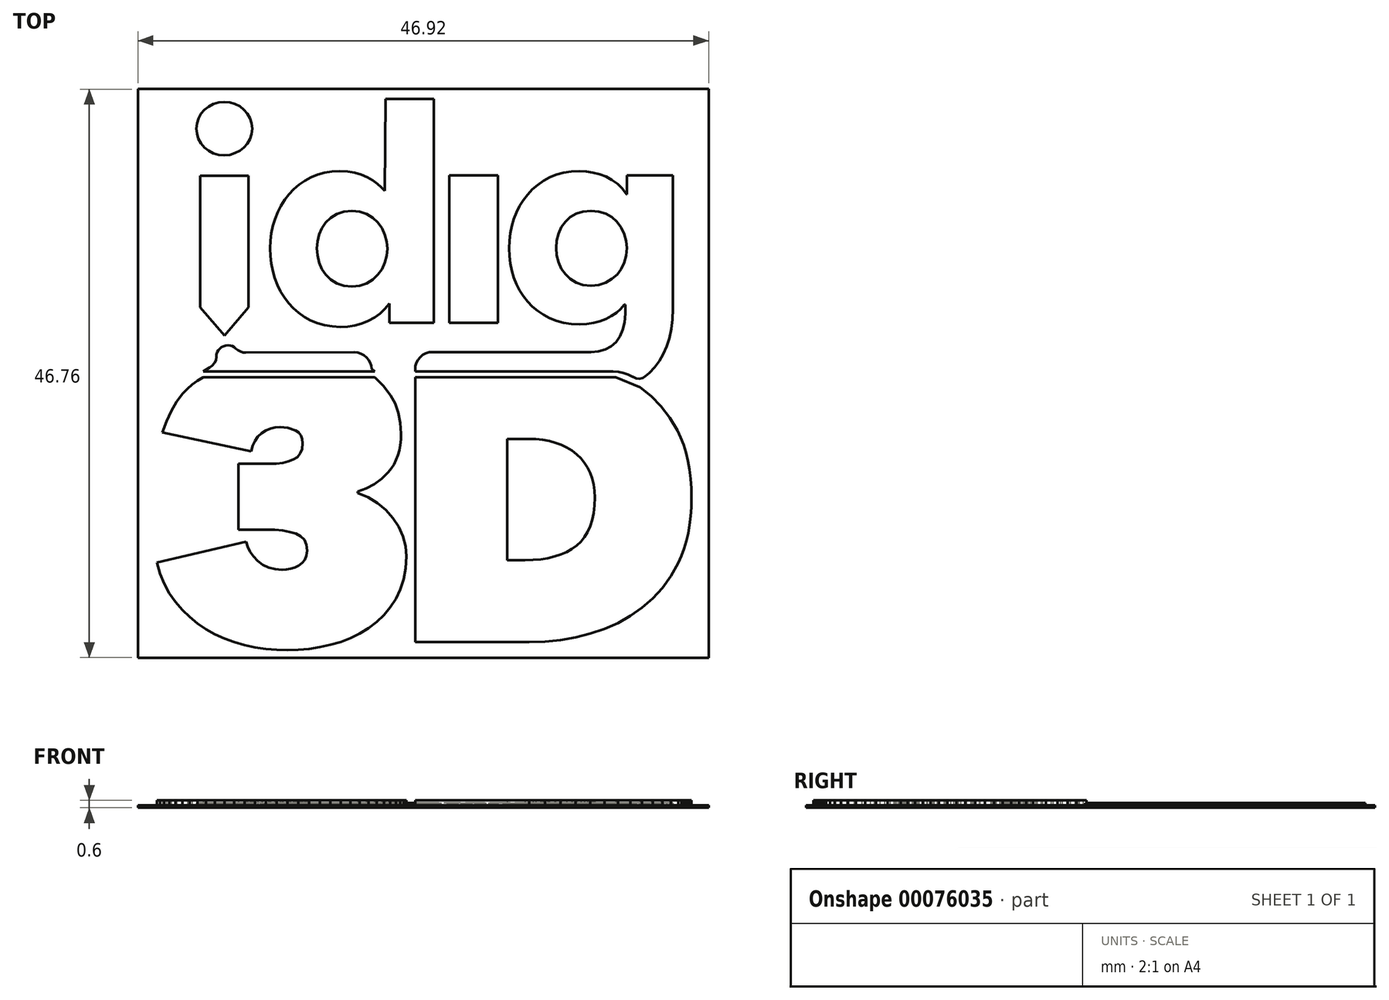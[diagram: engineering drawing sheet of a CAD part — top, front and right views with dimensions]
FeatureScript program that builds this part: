
annotation { "Feature Type Name" : "Feature", "Feature Type Description" : "" }
export const myFeature = defineFeature(function(context is Context, id is Id, definition is map)
    precondition{}
    {
        {
            var Q0;
            Q0=qCreatedBy(makeId("Top.planeOp"),FACE);
            var sketch = newSketch(context, id + "F0", { "sketchPlane" : qUnion([Q0])});
            skLineSegment(sketch, "E0", {"start": v(-3.12, 22.59) * mm, "end": v(0.88, 22.59) * mm});
            skLineSegment(sketch, "E1", {"start": v(0.88, 22.59) * mm, "end": v(0.88, 4.17) * mm});
            skLineSegment(sketch, "E2", {"start": v(17.03, -19.95) * mm, "end": v(16, -20.53) * mm});
            skLineSegment(sketch, "E3", {"start": v(12.5, -21.71) * mm, "end": v(11.27, -21.93) * mm});
            skLineSegment(sketch, "E4", {"start": v(14.9, -21.01) * mm, "end": v(13.73, -21.4) * mm});
            skLineSegment(sketch, "E5", {"start": v(-0.67, -22.1) * mm, "end": v(8.7, -22.1) * mm});
            skLineSegment(sketch, "E6", {"start": v(-3.17, 15) * mm, "end": v(-3.12, 22.59) * mm});
            skLineSegment(sketch, "E7", {"start": v(10, -22.06) * mm, "end": v(8.7, -22.1) * mm});
            skLineSegment(sketch, "E8", {"start": v(17.99, -19.28) * mm, "end": v(17.03, -19.95) * mm});
            skLineSegment(sketch, "E9", {"start": v(-21.3, -17.31) * mm, "end": v(-21.64, -16.47) * mm});
            skLineSegment(sketch, "E10", {"start": v(16, -20.53) * mm, "end": v(14.9, -21.01) * mm});
            skLineSegment(sketch, "E11", {"start": v(13.73, -21.4) * mm, "end": v(12.5, -21.71) * mm});
            skLineSegment(sketch, "E12", {"start": v(11.27, -21.93) * mm, "end": v(10, -22.06) * mm});
            skLineSegment(sketch, "E13", {"start": v(19.65, -17.64) * mm, "end": v(18.86, -18.5) * mm});
            skLineSegment(sketch, "E14", {"start": v(-18.56, -20.57) * mm, "end": v(-19.21, -20.04) * mm});
            skLineSegment(sketch, "E15", {"start": v(-16.35, -21.82) * mm, "end": v(-17.13, -21.46) * mm});
            skLineSegment(sketch, "E16", {"start": v(-11.18, -22.76) * mm, "end": v(-12.07, -22.74) * mm});
            skLineSegment(sketch, "E17", {"start": v(-9.4, -22.65) * mm, "end": v(-10.29, -22.73) * mm});
            skLineSegment(sketch, "E18", {"start": v(-7.64, -22.33) * mm, "end": v(-8.52, -22.52) * mm});
            skLineSegment(sketch, "E19", {"start": v(-15.54, -22.11) * mm, "end": v(-16.35, -21.82) * mm});
            skLineSegment(sketch, "E20", {"start": v(-0.67, -22.1) * mm, "end": v(-0.67, -0.31) * mm});
            skLineSegment(sketch, "E21", {"start": v(-10.29, -22.73) * mm, "end": v(-11.18, -22.76) * mm});
            skLineSegment(sketch, "E22", {"start": v(-5.98, -21.78) * mm, "end": v(-6.8, -22.09) * mm});
            skLineSegment(sketch, "E23", {"start": v(21.43, -14.42) * mm, "end": v(21.2, -15.02) * mm});
            skLineSegment(sketch, "E24", {"start": v(20.94, -15.6) * mm, "end": v(20.34, -16.67) * mm});
            skLineSegment(sketch, "E25", {"start": v(-14.7, -22.35) * mm, "end": v(-15.54, -22.11) * mm});
            skLineSegment(sketch, "E26", {"start": v(21.9, -12.46) * mm, "end": v(21.77, -13.14) * mm});
            skLineSegment(sketch, "E27", {"start": v(-20.38, -18.8) * mm, "end": v(-20.87, -18.09) * mm});
            skLineSegment(sketch, "E28", {"start": v(21.4, -5.87) * mm, "end": v(21.6, -6.52) * mm});
            skLineSegment(sketch, "E29", {"start": v(21.89, -7.91) * mm, "end": v(21.98, -8.66) * mm});
            skLineSegment(sketch, "E30", {"start": v(22.03, -9.45) * mm, "end": v(22.05, -10.28) * mm});
            skLineSegment(sketch, "E31", {"start": v(-21.64, -16.47) * mm, "end": v(-21.91, -15.56) * mm});
            skLineSegment(sketch, "E32", {"start": v(-21.91, -15.56) * mm, "end": v(-14.58, -13.84) * mm});
            skLineSegment(sketch, "E33", {"start": v(21.2, -15.02) * mm, "end": v(20.94, -15.6) * mm});
            skLineSegment(sketch, "E34", {"start": v(-6.8, -22.09) * mm, "end": v(-7.64, -22.33) * mm});
            skLineSegment(sketch, "E35", {"start": v(-13.82, -22.53) * mm, "end": v(-14.7, -22.35) * mm});
            skLineSegment(sketch, "E36", {"start": v(20.34, -16.67) * mm, "end": v(19.65, -17.64) * mm});
            skLineSegment(sketch, "E37", {"start": v(-8.52, -22.52) * mm, "end": v(-9.4, -22.65) * mm});
            skLineSegment(sketch, "E38", {"start": v(-19.21, -20.04) * mm, "end": v(-19.82, -19.45) * mm});
            skLineSegment(sketch, "E39", {"start": v(22.03, -11.03) * mm, "end": v(21.98, -11.76) * mm});
            skLineSegment(sketch, "E40", {"start": v(21.6, -6.52) * mm, "end": v(21.76, -7.2) * mm});
            skLineSegment(sketch, "E41", {"start": v(21.77, -13.14) * mm, "end": v(21.62, -13.8) * mm});
            skLineSegment(sketch, "E42", {"start": v(21.76, -7.2) * mm, "end": v(21.89, -7.91) * mm});
            skLineSegment(sketch, "E43", {"start": v(21.98, -8.66) * mm, "end": v(22.03, -9.45) * mm});
            skLineSegment(sketch, "E44", {"start": v(-20.87, -18.09) * mm, "end": v(-21.3, -17.31) * mm});
            skLineSegment(sketch, "E45", {"start": v(-12.95, -22.66) * mm, "end": v(-13.82, -22.53) * mm});
            skLineSegment(sketch, "E46", {"start": v(-17.87, -21.04) * mm, "end": v(-18.56, -20.57) * mm});
            skLineSegment(sketch, "E47", {"start": v(-3.84, -20.46) * mm, "end": v(-4.5, -20.96) * mm});
            skLineSegment(sketch, "E48", {"start": v(21.62, -13.8) * mm, "end": v(21.43, -14.42) * mm});
            skLineSegment(sketch, "E49", {"start": v(-5.22, -21.4) * mm, "end": v(-5.98, -21.78) * mm});
            skLineSegment(sketch, "E50", {"start": v(21.16, -5.27) * mm, "end": v(21.4, -5.87) * mm});
            skLineSegment(sketch, "E51", {"start": v(-19.82, -19.45) * mm, "end": v(-20.38, -18.8) * mm});
            skLineSegment(sketch, "E52", {"start": v(22.05, -10.28) * mm, "end": v(22.03, -11.03) * mm});
            skLineSegment(sketch, "E53", {"start": v(-12.07, -22.74) * mm, "end": v(-12.95, -22.66) * mm});
            skLineSegment(sketch, "E54", {"start": v(-1.68, -13.4) * mm, "end": v(-1.47, -14.21) * mm});
            skLineSegment(sketch, "E55", {"start": v(13.5, -13.04) * mm, "end": v(13.72, -12.57) * mm});
            skLineSegment(sketch, "E56", {"start": v(-1.4, -15.03) * mm, "end": v(-1.45, -16.02) * mm});
            skLineSegment(sketch, "E57", {"start": v(9.02, -15.34) * mm, "end": v(9.65, -15.29) * mm});
            skLineSegment(sketch, "E58", {"start": v(-1.62, -16.94) * mm, "end": v(-1.88, -17.78) * mm});
            skLineSegment(sketch, "E59", {"start": v(-17.13, -21.46) * mm, "end": v(-17.87, -21.04) * mm});
            skLineSegment(sketch, "E60", {"start": v(13.25, -13.46) * mm, "end": v(13.5, -13.04) * mm});
            skLineSegment(sketch, "E61", {"start": v(6.89, -15.36) * mm, "end": v(8.34, -15.36) * mm});
            skLineSegment(sketch, "E62", {"start": v(10.8, -15.06) * mm, "end": v(11.3, -14.9) * mm});
            skLineSegment(sketch, "E63", {"start": v(-2.26, -18.55) * mm, "end": v(-2.72, -19.25) * mm});
            skLineSegment(sketch, "E64", {"start": v(6.89, -5.39) * mm, "end": v(6.89, -15.36) * mm});
            skLineSegment(sketch, "E65", {"start": v(-3.25, -19.89) * mm, "end": v(-3.84, -20.46) * mm});
            skLineSegment(sketch, "E66", {"start": v(18.86, -18.5) * mm, "end": v(17.99, -19.28) * mm});
            skLineSegment(sketch, "E67", {"start": v(21.98, -11.76) * mm, "end": v(21.9, -12.46) * mm});
            skLineSegment(sketch, "E68", {"start": v(-4.5, -20.96) * mm, "end": v(-5.22, -21.4) * mm});
            skLineSegment(sketch, "E69", {"start": v(-1.98, -6.33) * mm, "end": v(-2.1, -6.74) * mm});
            skLineSegment(sketch, "E70", {"start": v(-14.75, 21.7) * mm, "end": v(-14.47, 21.38) * mm});
            skLineSegment(sketch, "E71", {"start": v(13.88, -12.05) * mm, "end": v(14, -11.49) * mm});
            skLineSegment(sketch, "E72", {"start": v(-18, 21.67) * mm, "end": v(-17.66, 21.94) * mm});
            skLineSegment(sketch, "E73", {"start": v(-17.27, 22.15) * mm, "end": v(-16.84, 22.28) * mm});
            skLineSegment(sketch, "E74", {"start": v(-2.72, -19.25) * mm, "end": v(-3.25, -19.89) * mm});
            skLineSegment(sketch, "E75", {"start": v(12.21, -14.44) * mm, "end": v(12.6, -14.16) * mm});
            skLineSegment(sketch, "E76", {"start": v(9.65, -15.29) * mm, "end": v(10.24, -15.2) * mm});
            skLineSegment(sketch, "E77", {"start": v(10.24, -15.2) * mm, "end": v(10.8, -15.06) * mm});
            skLineSegment(sketch, "E78", {"start": v(11.3, -14.9) * mm, "end": v(11.78, -14.69) * mm});
            skLineSegment(sketch, "E79", {"start": v(11.78, -14.69) * mm, "end": v(12.21, -14.44) * mm});
            skLineSegment(sketch, "E80", {"start": v(12.22, -6.36) * mm, "end": v(11.8, -6.1) * mm});
            skLineSegment(sketch, "E81", {"start": v(13.25, -7.36) * mm, "end": v(12.95, -7) * mm});
            skLineSegment(sketch, "E82", {"start": v(-18.66, 20.14) * mm, "end": v(-18.61, 20.57) * mm});
            skLineSegment(sketch, "E83", {"start": v(13.72, -12.57) * mm, "end": v(13.88, -12.05) * mm});
            skLineSegment(sketch, "E84", {"start": v(10.36, -5.57) * mm, "end": v(9.82, -5.47) * mm});
            skLineSegment(sketch, "E85", {"start": v(14.07, -10.87) * mm, "end": v(14.09, -10.21) * mm});
            skLineSegment(sketch, "E86", {"start": v(-15.91, 22.29) * mm, "end": v(-15.48, 22.16) * mm});
            skLineSegment(sketch, "E87", {"start": v(-1.88, -17.78) * mm, "end": v(-2.26, -18.55) * mm});
            skLineSegment(sketch, "E88", {"start": v(-17.26, 18.1) * mm, "end": v(-17.65, 18.3) * mm});
            skLineSegment(sketch, "E89", {"start": v(-16.84, 17.98) * mm, "end": v(-17.26, 18.1) * mm});
            skLineSegment(sketch, "E90", {"start": v(14.09, -10.21) * mm, "end": v(14.07, -9.66) * mm});
            skLineSegment(sketch, "E91", {"start": v(-14.26, 21) * mm, "end": v(-14.12, 20.58) * mm});
            skLineSegment(sketch, "E92", {"start": v(-18.28, 21.35) * mm, "end": v(-18, 21.67) * mm});
            skLineSegment(sketch, "E93", {"start": v(12.6, -14.16) * mm, "end": v(12.95, -13.83) * mm});
            skLineSegment(sketch, "E94", {"start": v(8.64, -5.39) * mm, "end": v(6.89, -5.39) * mm});
            skLineSegment(sketch, "E95", {"start": v(-14.37, 16.26) * mm, "end": v(-14.37, 5.44) * mm});
            skLineSegment(sketch, "E96", {"start": v(-18.36, 16.26) * mm, "end": v(-14.37, 16.26) * mm});
            skLineSegment(sketch, "E97", {"start": v(-18.36, 5.44) * mm, "end": v(-18.36, 16.26) * mm});
            skLineSegment(sketch, "E98", {"start": v(20.52, 16.3) * mm, "end": v(20.52, 5.31) * mm});
            skLineSegment(sketch, "E99", {"start": v(13.88, -8.64) * mm, "end": v(13.72, -8.18) * mm});
            skLineSegment(sketch, "E100", {"start": v(-21.45, -4.86) * mm, "end": v(-21.12, -3.94) * mm});
            skLineSegment(sketch, "E101", {"start": v(-14.15, -6.41) * mm, "end": v(-21.45, -4.86) * mm});
            skLineSegment(sketch, "E102", {"start": v(8.34, -15.36) * mm, "end": v(9.02, -15.34) * mm});
            skLineSegment(sketch, "E103", {"start": v(-14.08, 20.14) * mm, "end": v(-14.12, 19.69) * mm});
            skLineSegment(sketch, "E104", {"start": v(12.95, -13.83) * mm, "end": v(13.25, -13.46) * mm});
            skLineSegment(sketch, "E105", {"start": v(11.8, -6.1) * mm, "end": v(11.35, -5.89) * mm});
            skLineSegment(sketch, "E106", {"start": v(-16.37, 22.33) * mm, "end": v(-15.91, 22.29) * mm});
            skLineSegment(sketch, "E107", {"start": v(14.07, -9.66) * mm, "end": v(14, -9.13) * mm});
            skLineSegment(sketch, "E108", {"start": v(14, -9.13) * mm, "end": v(13.88, -8.64) * mm});
            skLineSegment(sketch, "E109", {"start": v(-16.37, 17.94) * mm, "end": v(-16.84, 17.98) * mm});
            skLineSegment(sketch, "E110", {"start": v(-15.91, 17.99) * mm, "end": v(-16.37, 17.94) * mm});
            skLineSegment(sketch, "E111", {"start": v(16.75, 16.3) * mm, "end": v(20.52, 16.3) * mm});
            skLineSegment(sketch, "E112", {"start": v(-18, 18.59) * mm, "end": v(-18.29, 18.93) * mm});
            skLineSegment(sketch, "E113", {"start": v(-18.49, 20.98) * mm, "end": v(-18.28, 21.35) * mm});
            skLineSegment(sketch, "E114", {"start": v(-14.12, 20.58) * mm, "end": v(-14.08, 20.14) * mm});
            skLineSegment(sketch, "E115", {"start": v(-18.61, 19.7) * mm, "end": v(-18.66, 20.14) * mm});
            skLineSegment(sketch, "E116", {"start": v(14, -11.49) * mm, "end": v(14.07, -10.87) * mm});
            skLineSegment(sketch, "E117", {"start": v(-9.6, -15) * mm, "end": v(-9.56, -14.57) * mm});
            skLineSegment(sketch, "E118", {"start": v(-10.57, -15.97) * mm, "end": v(-10.25, -15.8) * mm});
            skLineSegment(sketch, "E119", {"start": v(-10.48, -13.18) * mm, "end": v(-10.99, -13.04) * mm});
            skLineSegment(sketch, "E120", {"start": v(-13.6, -15.43) * mm, "end": v(-13.19, -15.75) * mm});
            skLineSegment(sketch, "E121", {"start": v(-2.5, -11.9) * mm, "end": v(-2.02, -12.62) * mm});
            skLineSegment(sketch, "E122", {"start": v(-12.2, 12.7) * mm, "end": v(-11.97, 13.27) * mm});
            skLineSegment(sketch, "E123", {"start": v(-3.76, -10.67) * mm, "end": v(-3.07, -11.24) * mm});
            skLineSegment(sketch, "E124", {"start": v(10.87, -5.7) * mm, "end": v(10.36, -5.57) * mm});
            skLineSegment(sketch, "E125", {"start": v(-1.45, -16.02) * mm, "end": v(-1.62, -16.94) * mm});
            skLineSegment(sketch, "E126", {"start": v(-14.44, -14.27) * mm, "end": v(-14.24, -14.67) * mm});
            skLineSegment(sketch, "E127", {"start": v(-10.99, -13.04) * mm, "end": v(-11.57, -12.94) * mm});
            skLineSegment(sketch, "E128", {"start": v(-1.47, -14.21) * mm, "end": v(-1.4, -15.03) * mm});
            skLineSegment(sketch, "E129", {"start": v(12.95, -7) * mm, "end": v(12.6, -6.66) * mm});
            skLineSegment(sketch, "E130", {"start": v(-16.84, 22.28) * mm, "end": v(-16.37, 22.33) * mm});
            skLineSegment(sketch, "E131", {"start": v(-11.97, 13.27) * mm, "end": v(-11.7, 13.8) * mm});
            skLineSegment(sketch, "E132", {"start": v(13.72, -8.18) * mm, "end": v(13.5, -7.76) * mm});
            skLineSegment(sketch, "E133", {"start": v(-12.96, -12.85) * mm, "end": v(-15.2, -12.85) * mm});
            skLineSegment(sketch, "E134", {"start": v(-15.2, -12.85) * mm, "end": v(-15.2, -7.44) * mm});
            skLineSegment(sketch, "E135", {"start": v(-15.48, 18.11) * mm, "end": v(-15.91, 17.99) * mm});
            skLineSegment(sketch, "E136", {"start": v(-17.66, 21.94) * mm, "end": v(-17.27, 22.15) * mm});
            skLineSegment(sketch, "E137", {"start": v(-17.65, 18.3) * mm, "end": v(-18, 18.59) * mm});
            skLineSegment(sketch, "E138", {"start": v(-14.47, 18.9) * mm, "end": v(-14.75, 18.58) * mm});
            skLineSegment(sketch, "E139", {"start": v(-14.26, 19.27) * mm, "end": v(-14.47, 18.9) * mm});
            skLineSegment(sketch, "E140", {"start": v(-18.5, 19.3) * mm, "end": v(-18.61, 19.7) * mm});
            skLineSegment(sketch, "E141", {"start": v(-10.08, -13.4) * mm, "end": v(-10.48, -13.18) * mm});
            skLineSegment(sketch, "E142", {"start": v(-10.66, 15.16) * mm, "end": v(-10.23, 15.53) * mm});
            skLineSegment(sketch, "E143", {"start": v(-6.54, 13.3) * mm, "end": v(-7.12, 13.1) * mm});
            skLineSegment(sketch, "E144", {"start": v(-9.76, 15.85) * mm, "end": v(-9.25, 16.13) * mm});
            skLineSegment(sketch, "E145", {"start": v(-8.7, 16.35) * mm, "end": v(-8.12, 16.51) * mm});
            skLineSegment(sketch, "E146", {"start": v(-21.12, -3.94) * mm, "end": v(-20.73, -3.1) * mm});
            skLineSegment(sketch, "E147", {"start": v(16.75, 14.74) * mm, "end": v(16.75, 16.3) * mm});
            skLineSegment(sketch, "E148", {"start": v(-3.74, 12.4) * mm, "end": v(-4.16, 12.8) * mm});
            skLineSegment(sketch, "E149", {"start": v(11.35, -5.89) * mm, "end": v(10.87, -5.7) * mm});
            skLineSegment(sketch, "E150", {"start": v(-12.19, -16.11) * mm, "end": v(-11.6, -16.16) * mm});
            skLineSegment(sketch, "E151", {"start": v(-9.62, -14.09) * mm, "end": v(-9.8, -13.7) * mm});
            skLineSegment(sketch, "E152", {"start": v(-9.98, -15.6) * mm, "end": v(-9.76, -15.33) * mm});
            skLineSegment(sketch, "E153", {"start": v(13.94, 16.53) * mm, "end": v(14.49, 16.38) * mm});
            skLineSegment(sketch, "E154", {"start": v(-12.22, -12.87) * mm, "end": v(-12.96, -12.85) * mm});
            skLineSegment(sketch, "E155", {"start": v(10.94, 16.35) * mm, "end": v(11.53, 16.51) * mm});
            skLineSegment(sketch, "E156", {"start": v(-14.24, -14.67) * mm, "end": v(-13.96, -15.06) * mm});
            skLineSegment(sketch, "E157", {"start": v(-14.47, 21.38) * mm, "end": v(-14.26, 21) * mm});
            skLineSegment(sketch, "E158", {"start": v(-3.17, 15) * mm, "end": v(-3.17, 15) * mm});
            skLineSegment(sketch, "E159", {"start": v(-4.6, 16.13) * mm, "end": v(-4.17, 15.87) * mm});
            skLineSegment(sketch, "E160", {"start": v(2.14, 4.17) * mm, "end": v(2.14, 16.3) * mm});
            skLineSegment(sketch, "E161", {"start": v(-12.5, 11.52) * mm, "end": v(-12.37, 12.12) * mm});
            skLineSegment(sketch, "E162", {"start": v(-3.07, -11.24) * mm, "end": v(-2.5, -11.9) * mm});
            skLineSegment(sketch, "E163", {"start": v(6.14, 16.3) * mm, "end": v(6.14, 4.17) * mm});
            skLineSegment(sketch, "E164", {"start": v(-11.7, 13.8) * mm, "end": v(-11.4, 14.29) * mm});
            skLineSegment(sketch, "E165", {"start": v(12.6, -6.66) * mm, "end": v(12.22, -6.36) * mm});
            skLineSegment(sketch, "E166", {"start": v(-10.23, 15.53) * mm, "end": v(-9.76, 15.85) * mm});
            skLineSegment(sketch, "E167", {"start": v(-14.75, 18.58) * mm, "end": v(-15.08, 18.32) * mm});
            skLineSegment(sketch, "E168", {"start": v(9.87, 15.83) * mm, "end": v(10.39, 16.12) * mm});
            skLineSegment(sketch, "E169", {"start": v(13.5, -7.76) * mm, "end": v(13.25, -7.36) * mm});
            skLineSegment(sketch, "E170", {"start": v(-2.02, -12.62) * mm, "end": v(-1.68, -13.4) * mm});
            skLineSegment(sketch, "E171", {"start": v(-14.12, 19.69) * mm, "end": v(-14.26, 19.27) * mm});
            skLineSegment(sketch, "E172", {"start": v(-18.29, 18.93) * mm, "end": v(-18.5, 19.3) * mm});
            skLineSegment(sketch, "E173", {"start": v(-5.87, 13.38) * mm, "end": v(-6.54, 13.3) * mm});
            skLineSegment(sketch, "E174", {"start": v(-18.61, 20.57) * mm, "end": v(-18.49, 20.98) * mm});
            skLineSegment(sketch, "E175", {"start": v(-14.58, -13.84) * mm, "end": v(-14.44, -14.27) * mm});
            skLineSegment(sketch, "E176", {"start": v(-15.23, 1.9) * mm, "end": v(-15.03, 1.8) * mm});
            skLineSegment(sketch, "E177", {"start": v(-10.35, -6.88) * mm, "end": v(-10.11, -6.58) * mm});
            skLineSegment(sketch, "E178", {"start": v(-4.16, 7.72) * mm, "end": v(-3.74, 8.11) * mm});
            skLineSegment(sketch, "E179", {"start": v(-8.57, 11.43) * mm, "end": v(-8.7, 10.86) * mm});
            skLineSegment(sketch, "E180", {"start": v(-8.75, 10.28) * mm, "end": v(-8.7, 9.7) * mm});
            skLineSegment(sketch, "E181", {"start": v(-11.73, 6.75) * mm, "end": v(-12, 7.28) * mm});
            skLineSegment(sketch, "E182", {"start": v(-14.37, 5.44) * mm, "end": v(-16.36, 3.12) * mm});
            skLineSegment(sketch, "E183", {"start": v(-15.71, 2.24) * mm, "end": v(-15.55, 2.16) * mm});
            skLineSegment(sketch, "E184", {"start": v(-2.24, -7.12) * mm, "end": v(-2.42, -7.48) * mm});
            skLineSegment(sketch, "E185", {"start": v(8.57, 14.72) * mm, "end": v(8.96, 15.13) * mm});
            skLineSegment(sketch, "E186", {"start": v(12.08, 12.85) * mm, "end": v(11.68, 12.47) * mm});
            skLineSegment(sketch, "E187", {"start": v(-7.12, 13.1) * mm, "end": v(-7.6, 12.8) * mm});
            skLineSegment(sketch, "E188", {"start": v(-9.26, 4.36) * mm, "end": v(-9.78, 4.65) * mm});
            skLineSegment(sketch, "E189", {"start": v(-3.16, 9.11) * mm, "end": v(-3, 9.68) * mm});
            skLineSegment(sketch, "E190", {"start": v(7.65, 13.25) * mm, "end": v(7.92, 13.77) * mm});
            skLineSegment(sketch, "E191", {"start": v(-4.02, -9.1) * mm, "end": v(-4.68, -9.45) * mm});
            skLineSegment(sketch, "E192", {"start": v(-20.73, -3.1) * mm, "end": v(-20.28, -2.33) * mm});
            skLineSegment(sketch, "E193", {"start": v(16.7, 14.74) * mm, "end": v(16.75, 14.74) * mm});
            skLineSegment(sketch, "E194", {"start": v(-12.57, 9.65) * mm, "end": v(-12.6, 10.28) * mm});
            skLineSegment(sketch, "E195", {"start": v(-5.64, 16.51) * mm, "end": v(-5.1, 16.35) * mm});
            skLineSegment(sketch, "E196", {"start": v(-4.54, -10.2) * mm, "end": v(-3.76, -10.67) * mm});
            skLineSegment(sketch, "E197", {"start": v(-12.18, -4.43) * mm, "end": v(-12.56, -4.53) * mm});
            skLineSegment(sketch, "E198", {"start": v(7.44, 12.7) * mm, "end": v(7.65, 13.25) * mm});
            skLineSegment(sketch, "E199", {"start": v(-3, 10.84) * mm, "end": v(-3.16, 11.4) * mm});
            skLineSegment(sketch, "E200", {"start": v(-3.74, 8.11) * mm, "end": v(-3.4, 8.58) * mm});
            skLineSegment(sketch, "E201", {"start": v(-10.11, -6.58) * mm, "end": v(-9.97, -6.2) * mm});
            skLineSegment(sketch, "E202", {"start": v(-8.02, 8.11) * mm, "end": v(-7.6, 7.72) * mm});
            skLineSegment(sketch, "E203", {"start": v(-12.72, -15.97) * mm, "end": v(-12.19, -16.11) * mm});
            skLineSegment(sketch, "E204", {"start": v(-8.7, 9.7) * mm, "end": v(-8.57, 9.12) * mm});
            skLineSegment(sketch, "E205", {"start": v(-19.76, -1.64) * mm, "end": v(-19.4, -1.26) * mm});
            skLineSegment(sketch, "E206", {"start": v(-17.6, 0.47) * mm, "end": v(-17.35, 0.65) * mm});
            skLineSegment(sketch, "E207", {"start": v(-2.63, -7.8) * mm, "end": v(-2.87, -8.11) * mm});
            skLineSegment(sketch, "E208", {"start": v(15.92, 12.46) * mm, "end": v(15.5, 12.84) * mm});
            skLineSegment(sketch, "E209", {"start": v(-11.57, -12.94) * mm, "end": v(-12.22, -12.87) * mm});
            skLineSegment(sketch, "E210", {"start": v(-16.36, 3.12) * mm, "end": v(-18.36, 5.44) * mm});
            skLineSegment(sketch, "E211", {"start": v(-3.78, 15.6) * mm, "end": v(-3.45, 15.3) * mm});
            skLineSegment(sketch, "E212", {"start": v(-5.23, 13.3) * mm, "end": v(-5.87, 13.38) * mm});
            skLineSegment(sketch, "E213", {"start": v(15.51, 15.92) * mm, "end": v(15.96, 15.59) * mm});
            skLineSegment(sketch, "E214", {"start": v(-15.2, -7.44) * mm, "end": v(-12.7, -7.44) * mm});
            skLineSegment(sketch, "E215", {"start": v(-8.02, 12.41) * mm, "end": v(-8.34, 11.95) * mm});
            skLineSegment(sketch, "E216", {"start": v(-5.1, 16.35) * mm, "end": v(-4.6, 16.13) * mm});
            skLineSegment(sketch, "E217", {"start": v(-10.25, -15.8) * mm, "end": v(-9.98, -15.6) * mm});
            skLineSegment(sketch, "E218", {"start": v(-9.56, -14.57) * mm, "end": v(-9.62, -14.09) * mm});
            skLineSegment(sketch, "E219", {"start": v(-14.59, 1.7) * mm, "end": v(-5.68, 1.73) * mm});
            skLineSegment(sketch, "E220", {"start": v(-2.1, -6.74) * mm, "end": v(-2.24, -7.12) * mm});
            skLineSegment(sketch, "E221", {"start": v(12.82, 16.64) * mm, "end": v(13.39, 16.61) * mm});
            skLineSegment(sketch, "E222", {"start": v(-15.48, 22.16) * mm, "end": v(-15.08, 21.96) * mm});
            skLineSegment(sketch, "E223", {"start": v(-10.25, 4.99) * mm, "end": v(-10.68, 5.36) * mm});
            skLineSegment(sketch, "E224", {"start": v(-4, 0.16) * mm, "end": v(-18.09, 0.16) * mm});
            skLineSegment(sketch, "E225", {"start": v(-9.25, 16.13) * mm, "end": v(-8.7, 16.35) * mm});
            skLineSegment(sketch, "E226", {"start": v(2.14, 16.3) * mm, "end": v(6.14, 16.3) * mm});
            skLineSegment(sketch, "E227", {"start": v(-11.13, -4.47) * mm, "end": v(-11.77, -4.4) * mm});
            skLineSegment(sketch, "E228", {"start": v(-12.56, -4.53) * mm, "end": v(-12.94, -4.69) * mm});
            skLineSegment(sketch, "E229", {"start": v(-12.1, -7.42) * mm, "end": v(-11.57, -7.35) * mm});
            skLineSegment(sketch, "E230", {"start": v(-15.08, 18.32) * mm, "end": v(-15.48, 18.11) * mm});
            skLineSegment(sketch, "E231", {"start": v(-13.96, -15.06) * mm, "end": v(-13.6, -15.43) * mm});
            skLineSegment(sketch, "E232", {"start": v(-11.4, 14.29) * mm, "end": v(-11.05, 14.74) * mm});
            skLineSegment(sketch, "E233", {"start": v(-12.37, 12.12) * mm, "end": v(-12.2, 12.7) * mm});
            skLineSegment(sketch, "E234", {"start": v(9.4, 15.5) * mm, "end": v(9.87, 15.83) * mm});
            skLineSegment(sketch, "E235", {"start": v(-18.56, -0.61) * mm, "end": v(-18.09, -0.31) * mm});
            skLineSegment(sketch, "E236", {"start": v(-12.5, 9.04) * mm, "end": v(-12.57, 9.65) * mm});
            skLineSegment(sketch, "E237", {"start": v(-3.42, -8.65) * mm, "end": v(-4.02, -9.1) * mm});
            skLineSegment(sketch, "E238", {"start": v(-8.7, 10.86) * mm, "end": v(-8.75, 10.28) * mm});
            skLineSegment(sketch, "E239", {"start": v(9.82, -5.47) * mm, "end": v(9.24, -5.4) * mm});
            skLineSegment(sketch, "E240", {"start": v(-1.85, -5.44) * mm, "end": v(-1.9, -5.9) * mm});
            skLineSegment(sketch, "E241", {"start": v(-10.68, -7.09) * mm, "end": v(-10.35, -6.88) * mm});
            skLineSegment(sketch, "E242", {"start": v(-3, 9.68) * mm, "end": v(-2.95, 10.26) * mm});
            skLineSegment(sketch, "E243", {"start": v(-12.57, 10.9) * mm, "end": v(-12.5, 11.52) * mm});
            skLineSegment(sketch, "E244", {"start": v(19.54, -2.7) * mm, "end": v(20.27, -3.64) * mm});
            skLineSegment(sketch, "E245", {"start": v(-17.02, 1.36) * mm, "end": v(-17, 1.56) * mm});
            skLineSegment(sketch, "E246", {"start": v(-5.4, -9.72) * mm, "end": v(-5.4, -9.85) * mm});
            skLineSegment(sketch, "E247", {"start": v(-7.6, 12.8) * mm, "end": v(-8.02, 12.41) * mm});
            skLineSegment(sketch, "E248", {"start": v(-15.41, 2.05) * mm, "end": v(-15.23, 1.9) * mm});
            skLineSegment(sketch, "E249", {"start": v(11.68, 12.47) * mm, "end": v(11.35, 12.02) * mm});
            skLineSegment(sketch, "E250", {"start": v(-10.52, -4.7) * mm, "end": v(-11.13, -4.47) * mm});
            skLineSegment(sketch, "E251", {"start": v(7.27, 12.11) * mm, "end": v(7.44, 12.7) * mm});
            skLineSegment(sketch, "E252", {"start": v(20.9, -4.7) * mm, "end": v(21.16, -5.27) * mm});
            skLineSegment(sketch, "E253", {"start": v(-10.91, -16.07) * mm, "end": v(-10.57, -15.97) * mm});
            skLineSegment(sketch, "E254", {"start": v(-7.6, 7.72) * mm, "end": v(-7.12, 7.4) * mm});
            skLineSegment(sketch, "E255", {"start": v(-4.16, 12.8) * mm, "end": v(-4.66, 13.1) * mm});
            skLineSegment(sketch, "E256", {"start": v(-17.35, 0.65) * mm, "end": v(-17.17, 0.84) * mm});
            skLineSegment(sketch, "E257", {"start": v(7.92, 13.77) * mm, "end": v(8.22, 14.26) * mm});
            skLineSegment(sketch, "E258", {"start": v(15.5, 12.84) * mm, "end": v(15, 13.13) * mm});
            skLineSegment(sketch, "E259", {"start": v(14.49, 16.38) * mm, "end": v(15.02, 16.18) * mm});
            skLineSegment(sketch, "E260", {"start": v(-19, -0.93) * mm, "end": v(-18.56, -0.61) * mm});
            skLineSegment(sketch, "E261", {"start": v(-12.2, 7.85) * mm, "end": v(-12.38, 8.44) * mm});
            skLineSegment(sketch, "E262", {"start": v(-9.76, -15.33) * mm, "end": v(-9.6, -15) * mm});
            skLineSegment(sketch, "E263", {"start": v(-5.23, 7.2) * mm, "end": v(-4.66, 7.4) * mm});
            skLineSegment(sketch, "E264", {"start": v(15.96, 15.59) * mm, "end": v(16.35, 15.2) * mm});
            skLineSegment(sketch, "E265", {"start": v(-3.16, 11.4) * mm, "end": v(-3.4, 11.93) * mm});
            skLineSegment(sketch, "E266", {"start": v(-2.42, -7.48) * mm, "end": v(-2.63, -7.8) * mm});
            skLineSegment(sketch, "E267", {"start": v(-8.57, 9.12) * mm, "end": v(-8.34, 8.59) * mm});
            skLineSegment(sketch, "E268", {"start": v(-18.09, -0.31) * mm, "end": v(-4, -0.31) * mm});
            skLineSegment(sketch, "E269", {"start": v(-9.78, 4.65) * mm, "end": v(-10.25, 4.99) * mm});
            skLineSegment(sketch, "E270", {"start": v(10.39, 16.12) * mm, "end": v(10.94, 16.35) * mm});
            skLineSegment(sketch, "E271", {"start": v(-20.28, -2.33) * mm, "end": v(-19.76, -1.64) * mm});
            skLineSegment(sketch, "E272", {"start": v(-15.08, 21.96) * mm, "end": v(-14.75, 21.7) * mm});
            skLineSegment(sketch, "E273", {"start": v(-8.12, 16.51) * mm, "end": v(-7.51, 16.6) * mm});
            skLineSegment(sketch, "E274", {"start": v(-14.03, -5.95) * mm, "end": v(-14.15, -6.41) * mm});
            skLineSegment(sketch, "E275", {"start": v(-12.94, -4.69) * mm, "end": v(-13.3, -4.91) * mm});
            skLineSegment(sketch, "E276", {"start": v(-11.08, 5.79) * mm, "end": v(-11.42, 6.25) * mm});
            skLineSegment(sketch, "E277", {"start": v(-11.42, 6.25) * mm, "end": v(-11.73, 6.75) * mm});
            skLineSegment(sketch, "E278", {"start": v(-8.34, 11.95) * mm, "end": v(-8.57, 11.43) * mm});
            skLineSegment(sketch, "E279", {"start": v(-11.05, 14.74) * mm, "end": v(-10.66, 15.16) * mm});
            skLineSegment(sketch, "E280", {"start": v(-3.45, 15.3) * mm, "end": v(-3.17, 15) * mm});
            skLineSegment(sketch, "E281", {"start": v(-9.8, -13.7) * mm, "end": v(-10.08, -13.4) * mm});
            skLineSegment(sketch, "E282", {"start": v(-4.17, 15.87) * mm, "end": v(-3.78, 15.6) * mm});
            skLineSegment(sketch, "E283", {"start": v(-12.38, 8.44) * mm, "end": v(-12.5, 9.04) * mm});
            skLineSegment(sketch, "E284", {"start": v(-11.1, -7.24) * mm, "end": v(-10.68, -7.09) * mm});
            skLineSegment(sketch, "E285", {"start": v(16.72, 10.3) * mm, "end": v(16.67, 10.9) * mm});
            skLineSegment(sketch, "E286", {"start": v(-12.6, 10.28) * mm, "end": v(-12.57, 10.9) * mm});
            skLineSegment(sketch, "E287", {"start": v(9.24, -5.4) * mm, "end": v(8.64, -5.39) * mm});
            skLineSegment(sketch, "E288", {"start": v(-16.07, 2.31) * mm, "end": v(-15.89, 2.3) * mm});
            skLineSegment(sketch, "E289", {"start": v(-4.68, -9.45) * mm, "end": v(-5.4, -9.72) * mm});
            skLineSegment(sketch, "E290", {"start": v(-10.26, -4.87) * mm, "end": v(-10.52, -4.7) * mm});
            skLineSegment(sketch, "E291", {"start": v(11.35, 12.02) * mm, "end": v(11.12, 11.5) * mm});
            skLineSegment(sketch, "E292", {"start": v(15.02, 16.18) * mm, "end": v(15.51, 15.92) * mm});
            skLineSegment(sketch, "E293", {"start": v(7.15, 11.52) * mm, "end": v(7.27, 12.11) * mm});
            skLineSegment(sketch, "E294", {"start": v(-11.6, -16.16) * mm, "end": v(-11.27, -16.14) * mm});
            skLineSegment(sketch, "E295", {"start": v(-18.09, 0.16) * mm, "end": v(-17.6, 0.47) * mm});
            skLineSegment(sketch, "E296", {"start": v(13.13, 13.32) * mm, "end": v(12.57, 13.13) * mm});
            skLineSegment(sketch, "E297", {"start": v(-7.12, 7.4) * mm, "end": v(-6.54, 7.2) * mm});
            skLineSegment(sketch, "E298", {"start": v(-5.87, 7.14) * mm, "end": v(-5.23, 7.2) * mm});
            skLineSegment(sketch, "E299", {"start": v(8.96, 15.13) * mm, "end": v(9.4, 15.5) * mm});
            skLineSegment(sketch, "E300", {"start": v(-1.9, -5.9) * mm, "end": v(-1.98, -6.33) * mm});
            skLineSegment(sketch, "E301", {"start": v(-2.87, -8.11) * mm, "end": v(-3.42, -8.65) * mm});
            skLineSegment(sketch, "E302", {"start": v(14.42, 13.32) * mm, "end": v(13.77, 13.38) * mm});
            skLineSegment(sketch, "E303", {"start": v(16.51, 11.48) * mm, "end": v(16.26, 12) * mm});
            skLineSegment(sketch, "E304", {"start": v(-10.68, 5.36) * mm, "end": v(-11.08, 5.79) * mm});
            skLineSegment(sketch, "E305", {"start": v(7.07, 10.9) * mm, "end": v(7.15, 11.52) * mm});
            skLineSegment(sketch, "E306", {"start": v(-14.81, 1.73) * mm, "end": v(-14.59, 1.7) * mm});
            skLineSegment(sketch, "E307", {"start": v(12.16, 16.6) * mm, "end": v(12.82, 16.64) * mm});
            skLineSegment(sketch, "E308", {"start": v(20.27, -3.64) * mm, "end": v(20.9, -4.7) * mm});
            skLineSegment(sketch, "E309", {"start": v(-3.4, 11.93) * mm, "end": v(-3.74, 12.4) * mm});
            skLineSegment(sketch, "E310", {"start": v(-3.4, 8.58) * mm, "end": v(-3.16, 9.11) * mm});
            skLineSegment(sketch, "E311", {"start": v(-12, 7.28) * mm, "end": v(-12.2, 7.85) * mm});
            skLineSegment(sketch, "E312", {"start": v(-8.7, 4.13) * mm, "end": v(-9.26, 4.36) * mm});
            skLineSegment(sketch, "E313", {"start": v(16.35, 15.2) * mm, "end": v(16.7, 14.74) * mm});
            skLineSegment(sketch, "E314", {"start": v(-19.4, -1.26) * mm, "end": v(-19, -0.93) * mm});
            skLineSegment(sketch, "E315", {"start": v(-13.3, -4.91) * mm, "end": v(-13.6, -5.2) * mm});
            skLineSegment(sketch, "E316", {"start": v(-13.85, -5.54) * mm, "end": v(-14.03, -5.95) * mm});
            skLineSegment(sketch, "E317", {"start": v(-6.23, 16.6) * mm, "end": v(-5.64, 16.51) * mm});
            skLineSegment(sketch, "E318", {"start": v(-8.34, 8.59) * mm, "end": v(-8.02, 8.11) * mm});
            skLineSegment(sketch, "E319", {"start": v(-4.66, 13.1) * mm, "end": v(-5.23, 13.3) * mm});
            skLineSegment(sketch, "E320", {"start": v(-2.95, 10.26) * mm, "end": v(-3, 10.84) * mm});
            skLineSegment(sketch, "E321", {"start": v(-6.87, 16.64) * mm, "end": v(-6.23, 16.6) * mm});
            skLineSegment(sketch, "E322", {"start": v(11.68, 8.15) * mm, "end": v(12.08, 7.77) * mm});
            skLineSegment(sketch, "E323", {"start": v(10.97, 9.7) * mm, "end": v(11.12, 9.14) * mm});
            skLineSegment(sketch, "E324", {"start": v(15.5, 7.76) * mm, "end": v(15.93, 8.14) * mm});
            skLineSegment(sketch, "E325", {"start": v(7.44, 7.88) * mm, "end": v(7.27, 8.46) * mm});
            skLineSegment(sketch, "E326", {"start": v(20.5, 4.45) * mm, "end": v(20.4, 3.65) * mm});
            skLineSegment(sketch, "E327", {"start": v(-16.26, 2.3) * mm, "end": v(-16.07, 2.31) * mm});
            skLineSegment(sketch, "E328", {"start": v(16.67, 10.9) * mm, "end": v(16.51, 11.48) * mm});
            skLineSegment(sketch, "E329", {"start": v(-9.97, -6.2) * mm, "end": v(-9.92, -5.75) * mm});
            skLineSegment(sketch, "E330", {"start": v(-10.07, -5.1) * mm, "end": v(-10.26, -4.87) * mm});
            skLineSegment(sketch, "E331", {"start": v(7.15, 9.05) * mm, "end": v(7.07, 9.66) * mm});
            skLineSegment(sketch, "E332", {"start": v(-5.4, -9.85) * mm, "end": v(-4.54, -10.2) * mm});
            skLineSegment(sketch, "E333", {"start": v(13.39, 16.61) * mm, "end": v(13.94, 16.53) * mm});
            skLineSegment(sketch, "E334", {"start": v(-13.19, -15.75) * mm, "end": v(-12.72, -15.97) * mm});
            skLineSegment(sketch, "E335", {"start": v(-6.54, 7.2) * mm, "end": v(-5.87, 7.14) * mm});
            skLineSegment(sketch, "E336", {"start": v(15, 13.13) * mm, "end": v(14.42, 13.32) * mm});
            skLineSegment(sketch, "E337", {"start": v(16.26, 8.59) * mm, "end": v(16.51, 9.11) * mm});
            skLineSegment(sketch, "E338", {"start": v(8.22, 14.26) * mm, "end": v(8.57, 14.72) * mm});
            skLineSegment(sketch, "E339", {"start": v(10.97, 10.92) * mm, "end": v(10.92, 10.3) * mm});
            skLineSegment(sketch, "E340", {"start": v(-17.06, 1.08) * mm, "end": v(-17.02, 1.36) * mm});
            skLineSegment(sketch, "E341", {"start": v(-4.66, 7.4) * mm, "end": v(-4.16, 7.72) * mm});
            skLineSegment(sketch, "E342", {"start": v(16.51, 9.11) * mm, "end": v(16.67, 9.7) * mm});
            skLineSegment(sketch, "E343", {"start": v(20.23, 2.9) * mm, "end": v(20.01, 2.22) * mm});
            skLineSegment(sketch, "E344", {"start": v(-15.03, 1.8) * mm, "end": v(-14.81, 1.73) * mm});
            skLineSegment(sketch, "E345", {"start": v(11.53, 16.51) * mm, "end": v(12.16, 16.6) * mm});
            skLineSegment(sketch, "E346", {"start": v(12.57, 13.13) * mm, "end": v(12.08, 12.85) * mm});
            skLineSegment(sketch, "E347", {"start": v(-13.6, -5.2) * mm, "end": v(-13.85, -5.54) * mm});
            skLineSegment(sketch, "E348", {"start": v(7.05, 10.28) * mm, "end": v(7.07, 10.9) * mm});
            skLineSegment(sketch, "E349", {"start": v(-7.51, 16.6) * mm, "end": v(-6.87, 16.64) * mm});
            skLineSegment(sketch, "E350", {"start": v(16.26, 12) * mm, "end": v(15.92, 12.46) * mm});
            skLineSegment(sketch, "E351", {"start": v(7.65, 7.33) * mm, "end": v(7.44, 7.88) * mm});
            skLineSegment(sketch, "E352", {"start": v(12.08, 7.77) * mm, "end": v(12.57, 7.47) * mm});
            skLineSegment(sketch, "E353", {"start": v(-15.89, 2.3) * mm, "end": v(-15.71, 2.24) * mm});
            skLineSegment(sketch, "E354", {"start": v(11.12, 9.14) * mm, "end": v(11.35, 8.6) * mm});
            skLineSegment(sketch, "E355", {"start": v(15.93, 8.14) * mm, "end": v(16.26, 8.59) * mm});
            skLineSegment(sketch, "E356", {"start": v(12.57, 7.47) * mm, "end": v(13.13, 7.28) * mm});
            skLineSegment(sketch, "E357", {"start": v(-12.7, -7.44) * mm, "end": v(-12.1, -7.42) * mm});
            skLineSegment(sketch, "E358", {"start": v(-11.27, -16.14) * mm, "end": v(-10.91, -16.07) * mm});
            skLineSegment(sketch, "E359", {"start": v(-9.96, -5.4) * mm, "end": v(-10.07, -5.1) * mm});
            skLineSegment(sketch, "E360", {"start": v(13.77, 13.38) * mm, "end": v(13.13, 13.32) * mm});
            skLineSegment(sketch, "E361", {"start": v(11.12, 11.5) * mm, "end": v(10.97, 10.92) * mm});
            skLineSegment(sketch, "E362", {"start": v(7.27, 8.46) * mm, "end": v(7.15, 9.05) * mm});
            skLineSegment(sketch, "E363", {"start": v(16.67, 9.7) * mm, "end": v(16.72, 10.3) * mm});
            skLineSegment(sketch, "E364", {"start": v(-17.17, 0.84) * mm, "end": v(-17.06, 1.08) * mm});
            skLineSegment(sketch, "E365", {"start": v(-1.88, -4.07) * mm, "end": v(-1.83, -4.96) * mm});
            skLineSegment(sketch, "E366", {"start": v(-16.44, 2.24) * mm, "end": v(-16.26, 2.3) * mm});
            skLineSegment(sketch, "E367", {"start": v(7.92, 6.82) * mm, "end": v(7.65, 7.33) * mm});
            skLineSegment(sketch, "E368", {"start": v(14.42, 7.28) * mm, "end": v(15, 7.47) * mm});
            skLineSegment(sketch, "E369", {"start": v(10.92, 10.3) * mm, "end": v(10.97, 9.7) * mm});
            skLineSegment(sketch, "E370", {"start": v(11.35, 8.6) * mm, "end": v(11.68, 8.15) * mm});
            skLineSegment(sketch, "E371", {"start": v(-11.77, -4.4) * mm, "end": v(-12.18, -4.43) * mm});
            skLineSegment(sketch, "E372", {"start": v(-11.57, -7.35) * mm, "end": v(-11.1, -7.24) * mm});
            skLineSegment(sketch, "E373", {"start": v(7.07, 9.66) * mm, "end": v(7.05, 10.28) * mm});
            skLineSegment(sketch, "E374", {"start": v(-16.6, 2.15) * mm, "end": v(-16.44, 2.24) * mm});
            skLineSegment(sketch, "E375", {"start": v(-1.83, -4.96) * mm, "end": v(-1.85, -5.44) * mm});
            skLineSegment(sketch, "E376", {"start": v(13.13, 7.28) * mm, "end": v(13.77, 7.21) * mm});
            skLineSegment(sketch, "E377", {"start": v(-9.92, -5.75) * mm, "end": v(-9.96, -5.4) * mm});
            skLineSegment(sketch, "E378", {"start": v(8.22, 6.34) * mm, "end": v(7.92, 6.82) * mm});
            skLineSegment(sketch, "E379", {"start": v(-17.02, 1.36) * mm, "end": v(-17.02, 1.36) * mm});
            skLineSegment(sketch, "E380", {"start": v(13.77, 7.21) * mm, "end": v(14.42, 7.28) * mm});
            skLineSegment(sketch, "E381", {"start": v(-2.04, -3.25) * mm, "end": v(-1.88, -4.07) * mm});
            skLineSegment(sketch, "E382", {"start": v(15, 7.47) * mm, "end": v(15.5, 7.76) * mm});
            skLineSegment(sketch, "E383", {"start": v(13.94, 0.16) * mm, "end": v(13.42, 0.16) * mm});
            skLineSegment(sketch, "E384", {"start": v(-0.64, 0.16) * mm, "end": v(-0.68, 0.16) * mm});
            skLineSegment(sketch, "E385", {"start": v(4.34, 1.76) * mm, "end": v(4.86, 1.76) * mm});
            skLineSegment(sketch, "E386", {"start": v(16.03, 0.13) * mm, "end": v(15.6, 0.16) * mm});
            skLineSegment(sketch, "E387", {"start": v(-4.67, 1.32) * mm, "end": v(-4.5, 1.11) * mm});
            skLineSegment(sketch, "E388", {"start": v(14.52, 4.3) * mm, "end": v(14, 4.15) * mm});
            skLineSegment(sketch, "E389", {"start": v(2.43, 1.76) * mm, "end": v(2.87, 1.76) * mm});
            skLineSegment(sketch, "E390", {"start": v(15.81, -0.31) * mm, "end": v(17.8, -1.15) * mm});
            skLineSegment(sketch, "E391", {"start": v(-7.49, 3.86) * mm, "end": v(-8.11, 3.96) * mm});
            skLineSegment(sketch, "E392", {"start": v(19, 0.5) * mm, "end": v(18.57, 0.04) * mm});
            skLineSegment(sketch, "E393", {"start": v(1.4, 0.16) * mm, "end": v(0.94, 0.16) * mm});
            skLineSegment(sketch, "E394", {"start": v(20.4, 3.65) * mm, "end": v(20.23, 2.9) * mm});
            skLineSegment(sketch, "E395", {"start": v(16.6, 4.92) * mm, "end": v(16.6, 5.65) * mm});
            skLineSegment(sketch, "E396", {"start": v(10.79, 1.76) * mm, "end": v(11.25, 1.76) * mm});
            skLineSegment(sketch, "E397", {"start": v(14.94, 1.97) * mm, "end": v(15.43, 2.23) * mm});
            skLineSegment(sketch, "E398", {"start": v(12.17, 4.08) * mm, "end": v(11.54, 4.17) * mm});
            skLineSegment(sketch, "E399", {"start": v(-6.82, 3.82) * mm, "end": v(-7.49, 3.86) * mm});
            skLineSegment(sketch, "E400", {"start": v(-4.01, 4.6) * mm, "end": v(-4.52, 4.32) * mm});
            skLineSegment(sketch, "E401", {"start": v(9.67, 0.16) * mm, "end": v(8.98, 0.16) * mm});
            skLineSegment(sketch, "E402", {"start": v(-0.26, 1.34) * mm, "end": v(-0.04, 1.52) * mm});
            skLineSegment(sketch, "E403", {"start": v(-4, -0.31) * mm, "end": v(-3.3, -1.01) * mm});
            skLineSegment(sketch, "E404", {"start": v(8.74, 1.76) * mm, "end": v(9.27, 1.76) * mm});
            skLineSegment(sketch, "E405", {"start": v(4.22, 0.16) * mm, "end": v(3.6, 0.16) * mm});
            skLineSegment(sketch, "E406", {"start": v(1.9, 0.16) * mm, "end": v(1.4, 0.16) * mm});
            skLineSegment(sketch, "E407", {"start": v(18.72, -1.87) * mm, "end": v(19.54, -2.7) * mm});
            skLineSegment(sketch, "E408", {"start": v(-2.8, 5.75) * mm, "end": v(-2.8, 4.17) * mm});
            skLineSegment(sketch, "E409", {"start": v(-2.31, -2.5) * mm, "end": v(-2.04, -3.25) * mm});
            skLineSegment(sketch, "E410", {"start": v(20.52, 5.31) * mm, "end": v(20.5, 4.45) * mm});
            skLineSegment(sketch, "E411", {"start": v(15.81, -0.31) * mm, "end": v(-0.67, -0.31) * mm});
            skLineSegment(sketch, "E412", {"start": v(17.8, -1.15) * mm, "end": v(18.72, -1.87) * mm});
            skLineSegment(sketch, "E413", {"start": v(9.87, 4.82) * mm, "end": v(9.4, 5.13) * mm});
            skLineSegment(sketch, "E414", {"start": v(0.88, 4.17) * mm, "end": v(-2.8, 4.17) * mm});
            skLineSegment(sketch, "E415", {"start": v(-15.55, 2.16) * mm, "end": v(-15.41, 2.05) * mm});
            skLineSegment(sketch, "E416", {"start": v(6.14, 4.17) * mm, "end": v(2.14, 4.17) * mm});
            skLineSegment(sketch, "E417", {"start": v(16.22, 5.3) * mm, "end": v(15.87, 5) * mm});
            skLineSegment(sketch, "E418", {"start": v(4.86, 0.16) * mm, "end": v(4.22, 0.16) * mm});
            skLineSegment(sketch, "E419", {"start": v(-4.3, 0.63) * mm, "end": v(-4.26, 0.37) * mm});
            skLineSegment(sketch, "E420", {"start": v(-0.35, 0.16) * mm, "end": v(-0.53, 0.16) * mm});
            skLineSegment(sketch, "E421", {"start": v(14.43, 0.16) * mm, "end": v(13.94, 0.16) * mm});
            skLineSegment(sketch, "E422", {"start": v(3.83, 1.76) * mm, "end": v(4.34, 1.76) * mm});
            skLineSegment(sketch, "E423", {"start": v(16.44, 0.05) * mm, "end": v(16.03, 0.13) * mm});
            skLineSegment(sketch, "E424", {"start": v(19.4, 1.01) * mm, "end": v(19, 0.5) * mm});
            skLineSegment(sketch, "E425", {"start": v(-4.89, 1.5) * mm, "end": v(-4.67, 1.32) * mm});
            skLineSegment(sketch, "E426", {"start": v(1.64, 1.76) * mm, "end": v(2.02, 1.76) * mm});
            skLineSegment(sketch, "E427", {"start": v(15.83, 2.58) * mm, "end": v(16.16, 3.03) * mm});
            skLineSegment(sketch, "E428", {"start": v(15.02, 4.48) * mm, "end": v(14.52, 4.3) * mm});
            skLineSegment(sketch, "E429", {"start": v(20.01, 2.22) * mm, "end": v(19.73, 1.59) * mm});
            skLineSegment(sketch, "E430", {"start": v(11.68, 1.76) * mm, "end": v(12.09, 1.76) * mm});
            skLineSegment(sketch, "E431", {"start": v(16.16, 3.03) * mm, "end": v(16.4, 3.57) * mm});
            skLineSegment(sketch, "E432", {"start": v(-0.44, 1.12) * mm, "end": v(-0.26, 1.34) * mm});
            skLineSegment(sketch, "E433", {"start": v(17.5, -0.4) * mm, "end": v(17.23, -0.3) * mm});
            skLineSegment(sketch, "E434", {"start": v(-4.52, 4.32) * mm, "end": v(-5.07, 4.1) * mm});
            skLineSegment(sketch, "E435", {"start": v(13.65, 1.76) * mm, "end": v(13.74, 1.76) * mm});
            skLineSegment(sketch, "E436", {"start": v(10.94, 4.33) * mm, "end": v(10.39, 4.54) * mm});
            skLineSegment(sketch, "E437", {"start": v(-6.22, 3.86) * mm, "end": v(-6.82, 3.82) * mm});
            skLineSegment(sketch, "E438", {"start": v(8.98, 0.16) * mm, "end": v(8.29, 0.16) * mm});
            skLineSegment(sketch, "E439", {"start": v(11.64, 0.16) * mm, "end": v(11, 0.16) * mm});
            skLineSegment(sketch, "E440", {"start": v(-2.69, -1.8) * mm, "end": v(-2.31, -2.5) * mm});
            skLineSegment(sketch, "E441", {"start": v(7.07, 1.76) * mm, "end": v(7.63, 1.76) * mm});
            skLineSegment(sketch, "E442", {"start": v(2.42, 0.16) * mm, "end": v(1.9, 0.16) * mm});
            skLineSegment(sketch, "E443", {"start": v(6.2, 0.16) * mm, "end": v(5.53, 0.16) * mm});
            skLineSegment(sketch, "E444", {"start": v(11, 0.16) * mm, "end": v(10.34, 0.16) * mm});
            skLineSegment(sketch, "E445", {"start": v(8.29, 0.16) * mm, "end": v(7.59, 0.16) * mm});
            skLineSegment(sketch, "E446", {"start": v(-16.86, 1.9) * mm, "end": v(-16.74, 2.03) * mm});
            skLineSegment(sketch, "E447", {"start": v(9.4, 5.13) * mm, "end": v(8.96, 5.5) * mm});
            skLineSegment(sketch, "E448", {"start": v(-3.3, -1.01) * mm, "end": v(-2.69, -1.8) * mm});
            skLineSegment(sketch, "E449", {"start": v(18.26, -0.23) * mm, "end": v(18.02, -0.37) * mm});
            skLineSegment(sketch, "E450", {"start": v(16.6, 5.65) * mm, "end": v(16.53, 5.65) * mm});
            skLineSegment(sketch, "E451", {"start": v(16.53, 5.65) * mm, "end": v(16.22, 5.3) * mm});
            skLineSegment(sketch, "E452", {"start": v(-5.14, 1.63) * mm, "end": v(-4.89, 1.5) * mm});
            skLineSegment(sketch, "E453", {"start": v(-0.57, 0.88) * mm, "end": v(-0.44, 1.12) * mm});
            skLineSegment(sketch, "E454", {"start": v(9.8, 1.76) * mm, "end": v(10.3, 1.76) * mm});
            skLineSegment(sketch, "E455", {"start": v(0.2, 1.65) * mm, "end": v(0.47, 1.73) * mm});
            skLineSegment(sketch, "E456", {"start": v(13.31, 1.76) * mm, "end": v(13.5, 1.76) * mm});
            skLineSegment(sketch, "E457", {"start": v(3.34, 1.76) * mm, "end": v(3.83, 1.76) * mm});
            skLineSegment(sketch, "E458", {"start": v(15.43, 2.23) * mm, "end": v(15.83, 2.58) * mm});
            skLineSegment(sketch, "E459", {"start": v(17.22, -0.3) * mm, "end": v(16.84, -0.1) * mm});
            skLineSegment(sketch, "E460", {"start": v(-4.5, 1.11) * mm, "end": v(-4.37, 0.88) * mm});
            skLineSegment(sketch, "E461", {"start": v(15.81, -0.31) * mm, "end": v(16.25, -0.55) * mm});
            skLineSegment(sketch, "E462", {"start": v(16.55, 4.2) * mm, "end": v(16.6, 4.92) * mm});
            skLineSegment(sketch, "E463", {"start": v(15.47, 4.72) * mm, "end": v(15.02, 4.48) * mm});
            skLineSegment(sketch, "E464", {"start": v(12.26, 0.16) * mm, "end": v(11.64, 0.16) * mm});
            skLineSegment(sketch, "E465", {"start": v(19.73, 1.59) * mm, "end": v(19.4, 1.01) * mm});
            skLineSegment(sketch, "E466", {"start": v(6.51, 1.76) * mm, "end": v(7.07, 1.76) * mm});
            skLineSegment(sketch, "E467", {"start": v(3.6, 0.16) * mm, "end": v(3, 0.16) * mm});
            skLineSegment(sketch, "E468", {"start": v(7.59, 0.16) * mm, "end": v(6.9, 0.16) * mm});
            skLineSegment(sketch, "E469", {"start": v(-5.07, 4.1) * mm, "end": v(-5.64, 3.95) * mm});
            skLineSegment(sketch, "E470", {"start": v(-5.64, 3.95) * mm, "end": v(-6.22, 3.86) * mm});
            skLineSegment(sketch, "E471", {"start": v(-16.94, 1.73) * mm, "end": v(-16.86, 1.9) * mm});
            skLineSegment(sketch, "E472", {"start": v(11.54, 4.17) * mm, "end": v(10.94, 4.33) * mm});
            skLineSegment(sketch, "E473", {"start": v(-3.56, 4.93) * mm, "end": v(-4.01, 4.6) * mm});
            skLineSegment(sketch, "E474", {"start": v(8.57, 5.9) * mm, "end": v(8.22, 6.34) * mm});
            skLineSegment(sketch, "E475", {"start": v(-0.04, 1.52) * mm, "end": v(0.2, 1.65) * mm});
            skLineSegment(sketch, "E476", {"start": v(-2.8, 5.75) * mm, "end": v(-3.18, 5.31) * mm});
            skLineSegment(sketch, "E477", {"start": v(-0.65, 0.61) * mm, "end": v(-0.57, 0.88) * mm});
            skLineSegment(sketch, "E478", {"start": v(-4.26, 0.37) * mm, "end": v(-4, 0.16) * mm});
            skLineSegment(sketch, "E479", {"start": v(13.74, 1.76) * mm, "end": v(13.77, 1.76) * mm});
            skLineSegment(sketch, "E480", {"start": v(17.23, -0.3) * mm, "end": v(17.22, -0.3) * mm});
            skLineSegment(sketch, "E481", {"start": v(13.44, 4.07) * mm, "end": v(12.85, 4.04) * mm});
            skLineSegment(sketch, "E482", {"start": v(1, 1.76) * mm, "end": v(1.3, 1.76) * mm});
            skLineSegment(sketch, "E483", {"start": v(12.86, 0.16) * mm, "end": v(12.26, 0.16) * mm});
            skLineSegment(sketch, "E484", {"start": v(15.87, 5) * mm, "end": v(15.47, 4.72) * mm});
            skLineSegment(sketch, "E485", {"start": v(-5.68, 1.73) * mm, "end": v(-5.4, 1.7) * mm});
            skLineSegment(sketch, "E486", {"start": v(6.9, 0.16) * mm, "end": v(6.2, 0.16) * mm});
            skLineSegment(sketch, "E487", {"start": v(5.96, 1.76) * mm, "end": v(6.51, 1.76) * mm});
            skLineSegment(sketch, "E488", {"start": v(3, 0.16) * mm, "end": v(2.42, 0.16) * mm});
            skLineSegment(sketch, "E489", {"start": v(12.09, 1.76) * mm, "end": v(12.45, 1.76) * mm});
            skLineSegment(sketch, "E490", {"start": v(17.76, -0.43) * mm, "end": v(17.5, -0.4) * mm});
            skLineSegment(sketch, "E491", {"start": v(18.57, 0.04) * mm, "end": v(18.26, -0.23) * mm});
            skLineSegment(sketch, "E492", {"start": v(-17, 1.56) * mm, "end": v(-16.94, 1.73) * mm});
            skLineSegment(sketch, "E493", {"start": v(12.85, 4.04) * mm, "end": v(12.17, 4.08) * mm});
            skLineSegment(sketch, "E494", {"start": v(5.53, 0.16) * mm, "end": v(4.86, 0.16) * mm});
            skLineSegment(sketch, "E495", {"start": v(10.34, 0.16) * mm, "end": v(9.67, 0.16) * mm});
            skLineSegment(sketch, "E496", {"start": v(8.96, 5.5) * mm, "end": v(8.57, 5.9) * mm});
            skLineSegment(sketch, "E497", {"start": v(-8.11, 3.96) * mm, "end": v(-8.7, 4.13) * mm});
            skLineSegment(sketch, "E498", {"start": v(-3.18, 5.31) * mm, "end": v(-3.56, 4.93) * mm});
            skLineSegment(sketch, "E499", {"start": v(13.5, 1.76) * mm, "end": v(13.65, 1.76) * mm});
            skLineSegment(sketch, "E500", {"start": v(-0.68, 0.16) * mm, "end": v(-0.68, 0.33) * mm});
            skLineSegment(sketch, "E501", {"start": v(13.42, 0.16) * mm, "end": v(12.86, 0.16) * mm});
            skLineSegment(sketch, "E502", {"start": v(0.18, 0.16) * mm, "end": v(-0.11, 0.16) * mm});
            skLineSegment(sketch, "E503", {"start": v(7.63, 1.76) * mm, "end": v(8.19, 1.76) * mm});
            skLineSegment(sketch, "E504", {"start": v(5.4, 1.76) * mm, "end": v(5.96, 1.76) * mm});
            skLineSegment(sketch, "E505", {"start": v(2.02, 1.76) * mm, "end": v(2.43, 1.76) * mm});
            skLineSegment(sketch, "E506", {"start": v(14, 4.15) * mm, "end": v(13.44, 4.07) * mm});
            skLineSegment(sketch, "E507", {"start": v(-4.37, 0.88) * mm, "end": v(-4.3, 0.63) * mm});
            skLineSegment(sketch, "E508", {"start": v(10.3, 1.76) * mm, "end": v(10.79, 1.76) * mm});
            skLineSegment(sketch, "E509", {"start": v(16.84, -0.1) * mm, "end": v(16.44, 0.05) * mm});
            skLineSegment(sketch, "E510", {"start": v(16.4, 3.57) * mm, "end": v(16.55, 4.2) * mm});
            skLineSegment(sketch, "E511", {"start": v(-5.4, 1.7) * mm, "end": v(-5.14, 1.63) * mm});
            skLineSegment(sketch, "E512", {"start": v(10.39, 4.54) * mm, "end": v(9.87, 4.82) * mm});
            skLineSegment(sketch, "E513", {"start": v(18.02, -0.37) * mm, "end": v(17.76, -0.43) * mm});
            skLineSegment(sketch, "E514", {"start": v(-16.74, 2.03) * mm, "end": v(-16.6, 2.15) * mm});
            skLineSegment(sketch, "E515", {"start": v(12.78, 1.76) * mm, "end": v(13.07, 1.76) * mm});
            skLineSegment(sketch, "E516", {"start": v(-0.53, 0.16) * mm, "end": v(-0.64, 0.16) * mm});
            skLineSegment(sketch, "E517", {"start": v(0.54, 0.16) * mm, "end": v(0.18, 0.16) * mm});
            skLineSegment(sketch, "E518", {"start": v(2.87, 1.76) * mm, "end": v(3.34, 1.76) * mm});
            skLineSegment(sketch, "E519", {"start": v(11.25, 1.76) * mm, "end": v(11.68, 1.76) * mm});
            skLineSegment(sketch, "E520", {"start": v(14.87, 0.16) * mm, "end": v(14.43, 0.16) * mm});
            skLineSegment(sketch, "E521", {"start": v(8.19, 1.76) * mm, "end": v(8.74, 1.76) * mm});
            skLineSegment(sketch, "E522", {"start": v(15.6, 0.16) * mm, "end": v(15.26, 0.16) * mm});
            skLineSegment(sketch, "E523", {"start": v(12.45, 1.76) * mm, "end": v(12.78, 1.76) * mm});
            skLineSegment(sketch, "E524", {"start": v(0.94, 0.16) * mm, "end": v(0.54, 0.16) * mm});
            skLineSegment(sketch, "E525", {"start": v(0.75, 1.76) * mm, "end": v(1, 1.76) * mm});
            skLineSegment(sketch, "E526", {"start": v(4.86, 1.76) * mm, "end": v(5.4, 1.76) * mm});
            skLineSegment(sketch, "E527", {"start": v(-0.11, 0.16) * mm, "end": v(-0.35, 0.16) * mm});
            skLineSegment(sketch, "E528", {"start": v(15.26, 0.16) * mm, "end": v(14.87, 0.16) * mm});
            skLineSegment(sketch, "E529", {"start": v(9.27, 1.76) * mm, "end": v(9.8, 1.76) * mm});
            skLineSegment(sketch, "E530", {"start": v(14.4, 1.81) * mm, "end": v(14.94, 1.97) * mm});
            skLineSegment(sketch, "E531", {"start": v(0.47, 1.73) * mm, "end": v(0.75, 1.76) * mm});
            skLineSegment(sketch, "E532", {"start": v(1.3, 1.76) * mm, "end": v(1.64, 1.76) * mm});
            skLineSegment(sketch, "E533", {"start": v(-0.68, 0.33) * mm, "end": v(-0.65, 0.61) * mm});
            skLineSegment(sketch, "E534", {"start": v(13.77, 1.76) * mm, "end": v(14.4, 1.81) * mm});
            skLineSegment(sketch, "E535", {"start": v(13.07, 1.76) * mm, "end": v(13.31, 1.76) * mm});
            skLineSegment(sketch, "E536.rect.bottom", {"start": v(-23.46, -23.38) * mm, "end": v(23.46, -23.38) * mm});
            skLineSegment(sketch, "E536.rect.left", {"start": v(-23.46, -23.38) * mm, "end": v(-23.46, 23.38) * mm});
            skLineSegment(sketch, "E536.rect.right", {"start": v(23.46, -23.38) * mm, "end": v(23.46, 23.38) * mm});
            skPoint(sketch, "E536.rect.middle", {"position": v(0, 0) * mm});
            skLineSegment(sketch, "E537", {"start": v(-23.46, 23.38) * mm, "end": v(23.46, 23.38) * mm});
            skSolve(sketch);
        }
        {
            var Q0;
            Q0=makeQuery(id+"F0.imprint","IMPRINT",FACE,{"disambiguationData":[TD([[makeQuery(id+"F0.imprint","IMPRINT",EDGE,{"derivedFrom":sQuery(id+"F0.wireOp",EDGE,"E9")}),-1.0]])]});
            var Q1;
            Q1=makeQuery(id+"F0.imprint","IMPRINT",FACE,{"disambiguationData":[TD([[makeQuery(id+"F0.imprint","IMPRINT",EDGE,{"derivedFrom":sQuery(id+"F0.wireOp",EDGE,"E55")}),1.0]])]});
            var Q2;
            Q2=makeQuery(id+"F0.imprint","IMPRINT",FACE,{"disambiguationData":[TD([[makeQuery(id+"F0.imprint","IMPRINT",EDGE,{"derivedFrom":sQuery(id+"F0.wireOp",EDGE,"E70")}),-1.0]])]});
            var Q3;
            Q3=makeQuery(id+"F0.imprint","IMPRINT",FACE,{"disambiguationData":[TD([[makeQuery(id+"F0.imprint","IMPRINT",EDGE,{"derivedFrom":sQuery(id+"F0.wireOp",EDGE,"E95")}),-1.0]])]});
            var Q4;
            Q4=makeQuery(id+"F0.imprint","IMPRINT",FACE,{"disambiguationData":[TD([[makeQuery(id+"F0.imprint","IMPRINT",EDGE,{"derivedFrom":sQuery(id+"F0.wireOp",EDGE,"E143")}),1.0]])]});
            var Q5;
            Q5=makeQuery(id+"F0.imprint","IMPRINT",FACE,{"disambiguationData":[TD([[makeQuery(id+"F0.imprint","IMPRINT",EDGE,{"derivedFrom":sQuery(id+"F0.wireOp",EDGE,"E160")}),-1.0]])]});
            var Q6;
            Q6=makeQuery(id+"F0.imprint","IMPRINT",FACE,{"disambiguationData":[TD([[makeQuery(id+"F0.imprint","IMPRINT",EDGE,{"derivedFrom":sQuery(id+"F0.wireOp",EDGE,"E176")}),-1.0]])]});
            var Q7;
            Q7=makeQuery(id+"F0.imprint","IMPRINT",FACE,{"disambiguationData":[TD([[makeQuery(id+"F0.imprint","IMPRINT",EDGE,{"derivedFrom":sQuery(id+"F0.wireOp",EDGE,"E186")}),1.0]])]});
            var Q8;
            Q8=makeQuery(id+"F0.imprint","IMPRINT",FACE,{"disambiguationData":[TD([[makeQuery(id+"F0.imprint","IMPRINT",EDGE,{"derivedFrom":sQuery(id+"F0.wireOp",EDGE,"E0")}),-1.0]])]});
            var Q9;
            Q9=makeQuery(id+"F0.imprint","IMPRINT",FACE,{"disambiguationData":[TD([[makeQuery(id+"F0.imprint","IMPRINT",EDGE,{"derivedFrom":sQuery(id+"F0.wireOp",EDGE,"E2")}),-1.0]])]});
            var Q10;
            Q10=makeQuery(id+"F0.imprint","IMPRINT",FACE,{"disambiguationData":[TD([[makeQuery(id+"F0.imprint","IMPRINT",EDGE,{"derivedFrom":sQuery(id+"F0.wireOp",EDGE,"E98")}),-1.0]])]});
            var Q11;
            Q11=makeQuery(id+"F0.imprint","IMPRINT",FACE,{"disambiguationData":[TD([[makeQuery(id+"F0.imprint","IMPRINT",EDGE,{"derivedFrom":sQuery(id+"F0.wireOp",EDGE,"E0")}),1.0]])]});
            extrude(context, id + "F1", {"entities" : qUnion([Q0, Q1, Q2, Q3, Q4, Q5, Q6, Q7, Q8, Q9, Q10, Q11]), "oppositeDirection" : true, "depth" : .2 * mm});
        }
        {
            var Q0;
            Q0=makeQuery(id+"F0.imprint","IMPRINT",FACE,{"disambiguationData":[TD([[makeQuery(id+"F0.imprint","IMPRINT",EDGE,{"derivedFrom":sQuery(id+"F0.wireOp",EDGE,"E70")}),-1.0]])]});
            var Q1;
            Q1=makeQuery(id+"F0.imprint","IMPRINT",FACE,{"disambiguationData":[TD([[makeQuery(id+"F0.imprint","IMPRINT",EDGE,{"derivedFrom":sQuery(id+"F0.wireOp",EDGE,"E0")}),-1.0]])]});
            var Q2;
            Q2=makeQuery(id+"F0.imprint","IMPRINT",FACE,{"disambiguationData":[TD([[makeQuery(id+"F0.imprint","IMPRINT",EDGE,{"derivedFrom":sQuery(id+"F0.wireOp",EDGE,"E160")}),-1.0]])]});
            var Q3;
            Q3=makeQuery(id+"F0.imprint","IMPRINT",FACE,{"disambiguationData":[TD([[makeQuery(id+"F0.imprint","IMPRINT",EDGE,{"derivedFrom":sQuery(id+"F0.wireOp",EDGE,"E98")}),-1.0]])]});
            var Q4;
            Q4=makeQuery(id+"F0.imprint","IMPRINT",FACE,{"disambiguationData":[TD([[makeQuery(id+"F0.imprint","IMPRINT",EDGE,{"derivedFrom":sQuery(id+"F0.wireOp",EDGE,"E176")}),-1.0]])]});
            var Q5;
            Q5=makeQuery(id+"F0.imprint","IMPRINT",FACE,{"disambiguationData":[TD([[makeQuery(id+"F0.imprint","IMPRINT",EDGE,{"derivedFrom":sQuery(id+"F0.wireOp",EDGE,"E95")}),-1.0]])]});
            extrude(context, id + "F2", {"entities" : qUnion([Q0, Q1, Q2, Q3, Q4, Q5]), "operationType" : NewBodyOperationType.ADD, "depth" : .2 * mm});
        }
        {
            var Q0;
            Q0=makeQuery(id+"F0.imprint","IMPRINT",FACE,{"disambiguationData":[TD([[makeQuery(id+"F0.imprint","IMPRINT",EDGE,{"derivedFrom":sQuery(id+"F0.wireOp",EDGE,"E2")}),-1.0]])]});
            var Q1;
            Q1=makeQuery(id+"F0.imprint","IMPRINT",FACE,{"disambiguationData":[TD([[makeQuery(id+"F0.imprint","IMPRINT",EDGE,{"derivedFrom":sQuery(id+"F0.wireOp",EDGE,"E9")}),-1.0]])]});
            extrude(context, id + "F3", {"entities" : qUnion([Q0, Q1]), "operationType" : NewBodyOperationType.ADD, "depth" : .4 * mm});
        }
    });
